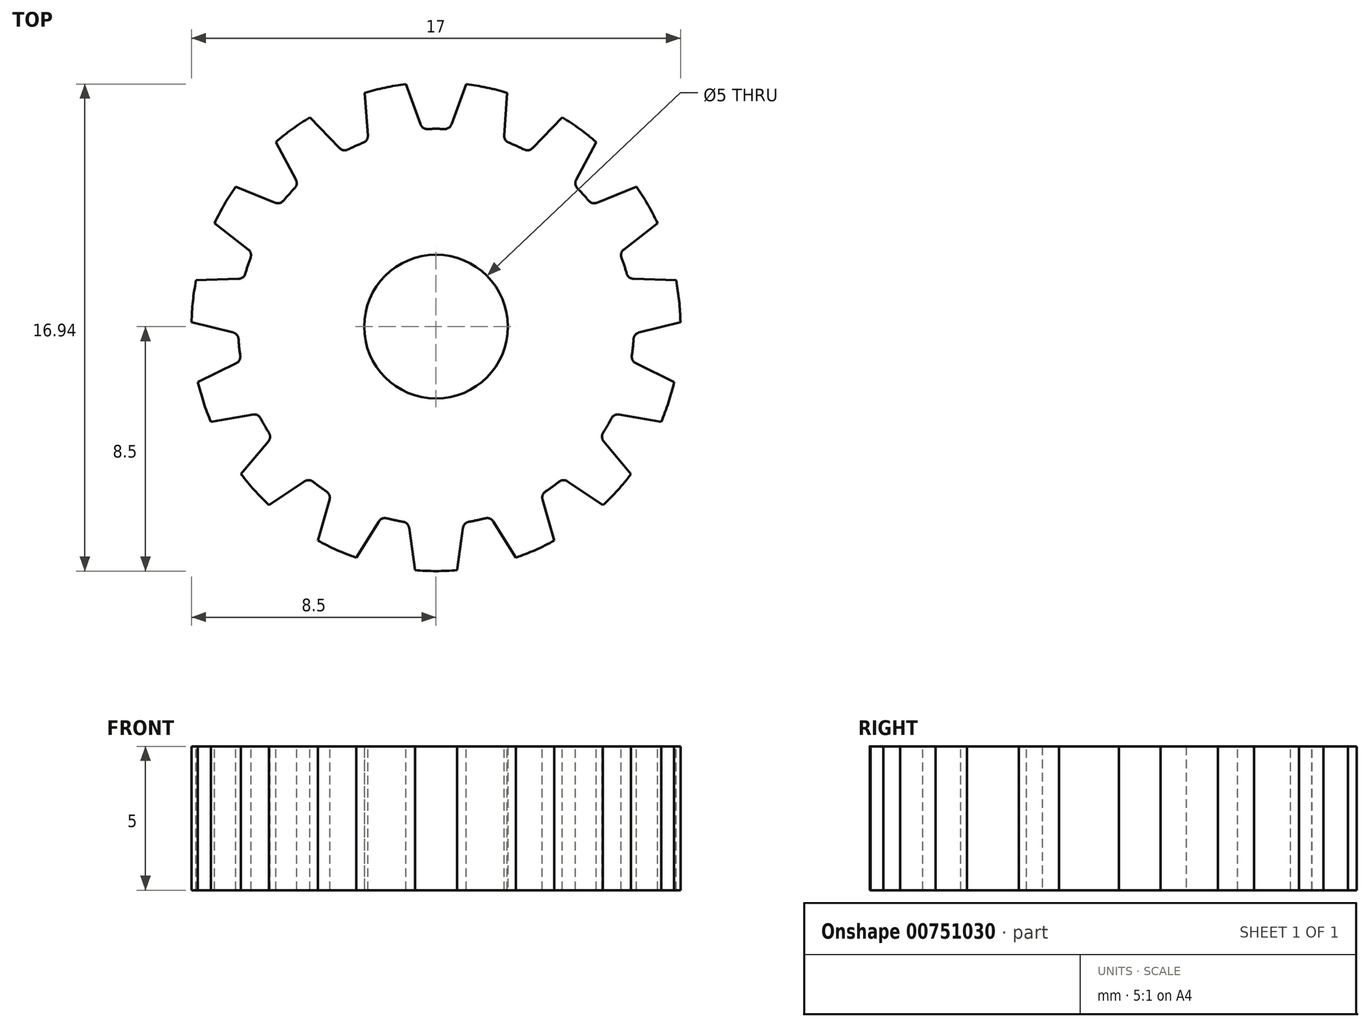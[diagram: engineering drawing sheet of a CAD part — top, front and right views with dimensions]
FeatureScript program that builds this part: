
annotation { "Feature Type Name" : "Feature", "Feature Type Description" : "" }
export const myFeature = defineFeature(function(context is Context, id is Id, definition is map)
    precondition{}
    {
        {
            var Q0;
            Q0=qCreatedBy(makeId("Top.planeOp"),FACE);
            var sketch = newSketch(context, id + "F0", { "sketchPlane" : qUnion([Q0])});
            skCircle(sketch, "E0", {"center": v(0, 0) * mm, "radius": 8.5 * mm});
            skCircle(sketch, "E1", {"center": v(0, 0) * mm, "radius": 2.5 * mm});
            skSolve(sketch);
        }
        {
            var Q0;
            Q0 = qSketchRegion(id + "F0", true);
            extrude(context, id + "F1", {"entities" : qUnion([Q0]), "depth" : 5 * mm, "offsetDistance" : 25 * mm});
        }
        {
            var Q0;
            Q0=makeQuery(id+"F1.opExtrude","CAP_FACE",FACE,{"disambiguationData":[OSD([sQuery(id+"F0.wireOp",EDGE,"E0"),sQuery(id+"F0.wireOp",EDGE,"E1")])],"isStart":false});
            var sketch = newSketch(context, id + "F2", { "sketchPlane" : qUnion([Q0])});
            skCircle(sketch, "E2", {"center": v(0, 0) * mm, "radius": 7.72 * mm, "construction": true});
            skCircle(sketch, "E3", {"center": v(0, 0) * mm, "radius": 6.88 * mm});
            skLineSegment(sketch, "E4", {"start": v(0.47, 6.87) * mm, "end": v(1.05, 8.44) * mm});
            skLineSegment(sketch, "E5", {"start": v(0, 7.72) * mm, "end": v(0.79, 7.72) * mm, "construction": true});
            skLineSegment(sketch, "E6.MirrorCS", {"start": v(-0.47, 6.87) * mm, "end": v(-1.05, 8.44) * mm});
            skSolve(sketch);
        }
        {
            var Q0;
            {var subQ0=sQuery(id+"F2.wireOp",EDGE,"E4");Q0=makeQuery(id+"F2.imprint","IMPRINT",FACE,{"disambiguationData":[TD([[makeQuery(id+"F2.imprint","IMPRINT",EDGE,{"derivedFrom":subQ0}),1.0]])]});}
            extrude(context, id + "F3", {"entities" : qUnion([Q0]), "operationType" : NewBodyOperationType.REMOVE, "oppositeDirection" : true, "depth" : 25 * mm, "offsetDistance" : 25 * mm});
        }
        {
            var Q0;
            Q0=makeQuery(id+"F3.boolean.opBoolean","COPY",EDGE,{"derivedFrom":makeQuery(id+"F3.opExtrude","SWEPT_EDGE",EDGE,{"disambiguationData":[OSD([sQuery(id+"F2.wireOp",EDGE,"E3"),sQuery(id+"F2.wireOp",EDGE,"E6.MirrorCS")])]})});
            var Q1;
            Q1=makeQuery(id+"F3.boolean.opBoolean","COPY",EDGE,{"derivedFrom":makeQuery(id+"F3.opExtrude","SWEPT_EDGE",EDGE,{"disambiguationData":[OSD([sQuery(id+"F0.wireOp",EDGE,"E0"),sQuery(id+"F2.wireOp",EDGE,"E6.MirrorCS")])]})});
            var Q2;
            Q2=makeQuery(id+"F3.boolean.opBoolean","COPY",EDGE,{"derivedFrom":makeQuery(id+"F3.opExtrude","SWEPT_EDGE",EDGE,{"disambiguationData":[OSD([sQuery(id+"F2.wireOp",EDGE,"E3"),sQuery(id+"F2.wireOp",EDGE,"E4")])]})});
            var Q3;
            Q3=makeQuery(id+"F3.boolean.opBoolean","COPY",EDGE,{"derivedFrom":makeQuery(id+"F3.opExtrude","SWEPT_EDGE",EDGE,{"disambiguationData":[OSD([sQuery(id+"F0.wireOp",EDGE,"E0"),sQuery(id+"F2.wireOp",EDGE,"E4")])]})});
            fillet(context, id + "F4", {"entities" : qUnion([Q0, Q1, Q2, Q3]), "radius" : 0.25 * mm, "tangentPropagation" : true, "allowEdgeOverflow" : false});
        }
        {
            var Q0;
            Q0=makeQuery(id+"F3.boolean.opBoolean","COPY",FACE,{"derivedFrom":makeQuery(id+"F3.opExtrude","SWEPT_FACE",FACE,{"disambiguationData":[OSD([sQuery(id+"F2.wireOp",EDGE,"E6.MirrorCS")])]})});
            var Q1;
            Q1=makeQuery(id+"F3.boolean.opBoolean","COPY",FACE,{"derivedFrom":makeQuery(id+"F3.opExtrude","SWEPT_FACE",FACE,{"disambiguationData":[OSD([sQuery(id+"F2.wireOp",EDGE,"E3")])]})});
            var Q2;
            Q2=makeQuery(id+"F3.boolean.opBoolean","COPY",FACE,{"derivedFrom":makeQuery(id+"F3.opExtrude","SWEPT_FACE",FACE,{"disambiguationData":[OSD([sQuery(id+"F2.wireOp",EDGE,"E4")])]})});
            var Q3;
            Q3=makeQuery(id+"F4.opFillet","BLEND_FACE",FACE,{"disambiguationData":[OSD([sQuery(id+"F2.wireOp",EDGE,"E3"),sQuery(id+"F2.wireOp",EDGE,"E6.MirrorCS")])]});
            var Q4;
            Q4=makeQuery(id+"F4.opFillet","BLEND_FACE",FACE,{"disambiguationData":[OSD([sQuery(id+"F2.wireOp",EDGE,"E3"),sQuery(id+"F2.wireOp",EDGE,"E4")])]});
            var Q5;
            Q5=makeQuery(id+"F4.opFillet","BLEND_FACE",FACE,{"disambiguationData":[OSD([sQuery(id+"F0.wireOp",EDGE,"E0"),sQuery(id+"F2.wireOp",EDGE,"E4")])]});
            var Q6;
            Q6=makeQuery(id+"F4.opFillet","BLEND_FACE",FACE,{"disambiguationData":[OSD([sQuery(id+"F0.wireOp",EDGE,"E0"),sQuery(id+"F2.wireOp",EDGE,"E6.MirrorCS")])]});
            var Q7;
            Q7=makeQuery(id+"F1.opExtrude","SWEPT_FACE",FACE,{"disambiguationData":[OSD([sQuery(id+"F0.wireOp",EDGE,"E0")])]});
            circularPattern(context, id + "F5", {"patternType" : PatternType.FACE, "faces" : qUnion([Q0, Q1, Q2, Q3, Q4, Q5, Q6]), "axis" : qUnion([Q7]), "angle" : 360 * degree, "instanceCount" : 15, "equalSpace" : true});
        }
    });
